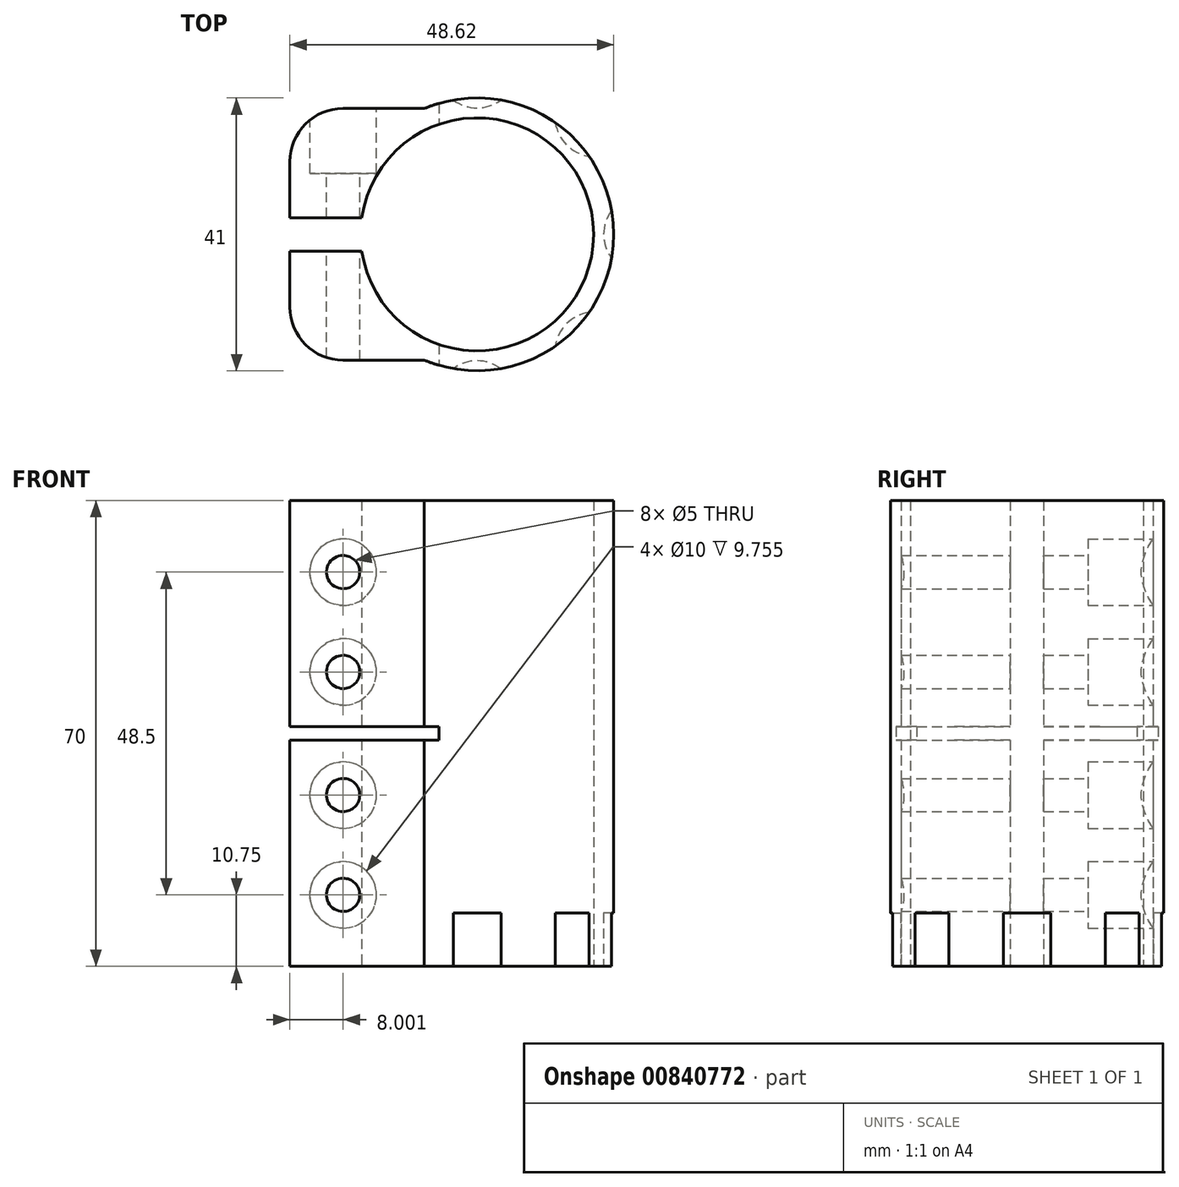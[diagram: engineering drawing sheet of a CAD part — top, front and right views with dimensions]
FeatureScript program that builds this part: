
annotation { "Feature Type Name" : "Feature", "Feature Type Description" : "" }
export const myFeature = defineFeature(function(context is Context, id is Id, definition is map)
    precondition{}
    {
        {
            var Q0;
            Q0=qCreatedBy(makeId("Top.planeOp"),FACE);
            var sketch = newSketch(context, id + "F0", { "sketchPlane" : qUnion([Q0])});
            skArc(sketch, "E0", {"start": v(-17.32, -2.5) * mm, "mid": v(17.5, 0) * mm, "end": v(-17.32, 2.5) * mm});
            skArc(sketch, "E1", {"start": v(-7.92, -18.9) * mm, "mid": v(20.5, 0) * mm, "end": v(-7.92, 18.9) * mm});
            skLineSegment(sketch, "E2", {"start": v(-17.32, 2.5) * mm, "end": v(-28.12, 2.5) * mm});
            skLineSegment(sketch, "E3", {"start": v(-28.12, 2.5) * mm, "end": v(-28.12, 10.9) * mm});
            skLineSegment(sketch, "E4", {"start": v(-20.12, 18.9) * mm, "end": v(-7.92, 18.9) * mm});
            skPoint(sketch, "E5.visualSharp", {"position": v(-28.12, 18.9) * mm});
            skArc(sketch, "E5.filletArc", {"start": v(-20.12, 18.9) * mm, "mid": v(-25.78, 16.57) * mm, "end": v(-28.12, 10.9) * mm});
            skLineSegment(sketch, "E6", {"start": v(0, 0) * mm, "end": v(38.47, 0) * mm, "construction": true});
            skLineSegment(sketch, "E7.MirrorCS", {"start": v(-20.12, -18.9) * mm, "end": v(-7.92, -18.9) * mm});
            skArc(sketch, "E8.MirrorCS", {"start": v(-20.12, -18.9) * mm, "mid": v(-25.78, -16.57) * mm, "end": v(-28.12, -10.9) * mm});
            skLineSegment(sketch, "E9.MirrorCS", {"start": v(-28.12, -2.5) * mm, "end": v(-28.12, -10.9) * mm});
            skLineSegment(sketch, "E10.MirrorCS", {"start": v(-17.32, -2.5) * mm, "end": v(-28.12, -2.5) * mm});
            skSolve(sketch);
        }
        {
            var Q0;
            Q0=makeQuery(id+"F0.imprint","IMPRINT",FACE,{"disambiguationData":[TD([[makeQuery(id+"F0.imprint","IMPRINT",EDGE,{"derivedFrom":sQuery(id+"F0.wireOp",EDGE,"E0")}),-1.0]])]});
            extrude(context, id + "F1", {"entities" : qUnion([Q0]), "endBound" : BoundingType.SYMMETRIC, "depth" : 70 * mm, "offsetDistance" : 25 * mm});
        }
        {
            var Q0;
            Q0=makeQuery(id+"F1.opExtrude","SWEPT_FACE",FACE,{"disambiguationData":[OSD([sQuery(id+"F0.wireOp",EDGE,"E4")])]});
            var sketch = newSketch(context, id + "F2", { "sketchPlane" : qUnion([Q0])});
            skPoint(sketch, "E11", {"position": v(20.12, -24.25) * mm});
            skPoint(sketch, "E12", {"position": v(20.12, -9.25) * mm});
            skPoint(sketch, "E13", {"position": v(20.12, 9.25) * mm});
            skPoint(sketch, "E14", {"position": v(20.12, 24.25) * mm});
            skSolve(sketch);
        }
        {
            var Q0;
            Q0=sQuery(id+"F2.wireOp",VERTEX,"E11");
            var Q1;
            Q1=sQuery(id+"F2.wireOp",VERTEX,"E12");
            var Q2;
            Q2=sQuery(id+"F2.wireOp",VERTEX,"E13");
            var Q3;
            Q3=sQuery(id+"F2.wireOp",VERTEX,"E14");
            var Q4;
            Q4=makeQuery(id+"F1.opExtrude","SWEPT_BODY",BODY,{"disambiguationData":[OSD([sQuery(id+"F0.wireOp",EDGE,"E0"),sQuery(id+"F0.wireOp",EDGE,"E1"),sQuery(id+"F0.wireOp",EDGE,"E2"),sQuery(id+"F0.wireOp",EDGE,"E3"),sQuery(id+"F0.wireOp",EDGE,"E4"),sQuery(id+"F0.wireOp",EDGE,"E5.filletArc"),sQuery(id+"F0.wireOp",EDGE,"E7.MirrorCS"),sQuery(id+"F0.wireOp",EDGE,"E8.MirrorCS"),sQuery(id+"F0.wireOp",EDGE,"E9.MirrorCS"),sQuery(id+"F0.wireOp",EDGE,"E10.MirrorCS")])]});
            hole(context, id + "F3", {"style" : HoleStyle.C_BORE, "endStyle" : HoleEndStyle.THROUGH, "holeDiameter" : 5 * mm, "cBoreDiameter" : 10 * mm, "cBoreDepth" : 8 * mm, "majorDiameter" : 5 * mm, "isTappedThrough" : true, "tappedDepth" : 12 * mm, "tapClearance" : 3, "locations" : qUnion([Q0, Q1, Q2, Q3]), "scope" : qUnion([Q4])});
        }
        {
            var Q0;
            Q0=qCreatedBy(makeId("Front.planeOp"),FACE);
            var sketch = newSketch(context, id + "F4", { "sketchPlane" : qUnion([Q0])});
            skPoint(sketch, "E15.right.end.orphan", {"position": v(-1.39, 0.57) * mm});
            skPoint(sketch, "E15.right.start.orphan", {"position": v(-1.39, -0.6) * mm});
            skPoint(sketch, "E15.left.start.orphan", {"position": v(-14.56, -0.6) * mm});
            skLineSegment(sketch, "E16.bottom", {"start": v(-28.12, -1) * mm, "end": v(-5.72, -1) * mm});
            skLineSegment(sketch, "E16.top", {"start": v(-28.12, 1) * mm, "end": v(-5.72, 1) * mm});
            skLineSegment(sketch, "E16.left", {"start": v(-28.12, -1) * mm, "end": v(-28.12, 1) * mm});
            skLineSegment(sketch, "E16.right", {"start": v(-5.72, -1) * mm, "end": v(-5.72, 1) * mm});
            skSolve(sketch);
        }
        {
            var Q0;
            Q0=makeQuery(id+"F4.imprint","IMPRINT",FACE,{"disambiguationData":[TD([[makeQuery(id+"F4.imprint","IMPRINT",EDGE,{"derivedFrom":sQuery(id+"F4.wireOp",EDGE,"E16.bottom")}),1.0]])]});
            extrude(context, id + "F5", {"entities" : qUnion([Q0]), "operationType" : NewBodyOperationType.REMOVE, "endBound" : BoundingType.SYMMETRIC, "oppositeDirection" : true, "depth" : 50 * mm, "offsetDistance" : 25 * mm});
        }
        {
            var Q0;
            Q0=makeQuery(id+"F1.opExtrude","CAP_FACE",FACE,{"disambiguationData":[OSD([sQuery(id+"F0.wireOp",EDGE,"E0"),sQuery(id+"F0.wireOp",EDGE,"E1"),sQuery(id+"F0.wireOp",EDGE,"E2"),sQuery(id+"F0.wireOp",EDGE,"E3"),sQuery(id+"F0.wireOp",EDGE,"E4"),sQuery(id+"F0.wireOp",EDGE,"E5.filletArc"),sQuery(id+"F0.wireOp",EDGE,"E7.MirrorCS"),sQuery(id+"F0.wireOp",EDGE,"E8.MirrorCS"),sQuery(id+"F0.wireOp",EDGE,"E9.MirrorCS"),sQuery(id+"F0.wireOp",EDGE,"E10.MirrorCS")])],"isStart":true});
            var sketch = newSketch(context, id + "F6", { "sketchPlane" : qUnion([Q0])});
            skCircle(sketch, "E17", {"center": v(0, -25) * mm, "radius": 6 * mm});
            skCircle(sketch, "E18.1.0", {"center": v(17.68, -17.68) * mm, "radius": 6 * mm});
            skCircle(sketch, "E18.2.0", {"center": v(25, 0) * mm, "radius": 6 * mm});
            skCircle(sketch, "E18.3.0", {"center": v(17.68, 17.68) * mm, "radius": 6 * mm});
            skCircle(sketch, "E18.4.0", {"center": v(0, 25) * mm, "radius": 6 * mm});
            skPoint(sketch, "E18.center", {"position": v(0, 0) * mm});
            skLineSegment(sketch, "E18.anchor1", {"start": v(0, 0) * mm, "end": v(0, -25) * mm, "construction": true});
            skLineSegment(sketch, "E18.anchor2", {"start": v(0, 0) * mm, "end": v(0, 25) * mm, "construction": true});
            skSolve(sketch);
        }
        {
            var Q0;
            {var subQ0=sQuery(id+"F6.wireOp",EDGE,"E18.4.0");var subQ1=makeQuery(id+"F1.opExtrude","CAP_EDGE",EDGE,{"disambiguationData":[OSD([sQuery(id+"F0.wireOp",EDGE,"E1")])],"isStart":true});var subQ2=makeQuery(id+"F6.imprint","INTERSECT",VERTEX,{"disambiguationData":[OD(0.0)],"derivedFrom":[subQ1,subQ0]});Q0=makeQuery(id+"F6.imprint","IMPRINT",FACE,{"disambiguationData":[TD([[makeQuery(id+"F6.imprint","IMPRINT",EDGE,{"disambiguationData":[TD([[subQ2,1.0]])],"derivedFrom":subQ0}),1.0]])]});}
            var Q1;
            {var subQ0=sQuery(id+"F6.wireOp",EDGE,"E18.3.0");var subQ1=makeQuery(id+"F1.opExtrude","CAP_EDGE",EDGE,{"disambiguationData":[OSD([sQuery(id+"F0.wireOp",EDGE,"E1")])],"isStart":true});var subQ2=makeQuery(id+"F6.imprint","INTERSECT",VERTEX,{"disambiguationData":[OD(0.0)],"derivedFrom":[subQ1,subQ0]});Q1=makeQuery(id+"F6.imprint","IMPRINT",FACE,{"disambiguationData":[TD([[makeQuery(id+"F6.imprint","IMPRINT",EDGE,{"disambiguationData":[TD([[subQ2,1.0]])],"derivedFrom":subQ0}),1.0]])]});}
            var Q2;
            {var subQ0=sQuery(id+"F6.wireOp",EDGE,"E18.2.0");var subQ1=makeQuery(id+"F1.opExtrude","CAP_EDGE",EDGE,{"disambiguationData":[OSD([sQuery(id+"F0.wireOp",EDGE,"E1")])],"isStart":true});var subQ2=makeQuery(id+"F6.imprint","INTERSECT",VERTEX,{"disambiguationData":[OD(0.0)],"derivedFrom":[subQ1,subQ0]});Q2=makeQuery(id+"F6.imprint","IMPRINT",FACE,{"disambiguationData":[TD([[makeQuery(id+"F6.imprint","IMPRINT",EDGE,{"disambiguationData":[TD([[subQ2,-1.0]])],"derivedFrom":subQ0}),1.0]])]});}
            var Q3;
            {var subQ0=sQuery(id+"F6.wireOp",EDGE,"E18.1.0");var subQ1=makeQuery(id+"F1.opExtrude","CAP_EDGE",EDGE,{"disambiguationData":[OSD([sQuery(id+"F0.wireOp",EDGE,"E1")])],"isStart":true});var subQ2=makeQuery(id+"F6.imprint","INTERSECT",VERTEX,{"disambiguationData":[OD(0.0)],"derivedFrom":[subQ1,subQ0]});Q3=makeQuery(id+"F6.imprint","IMPRINT",FACE,{"disambiguationData":[TD([[makeQuery(id+"F6.imprint","IMPRINT",EDGE,{"disambiguationData":[TD([[subQ2,-1.0]])],"derivedFrom":subQ0}),1.0]])]});}
            var Q4;
            {var subQ0=sQuery(id+"F6.wireOp",EDGE,"E17");var subQ1=makeQuery(id+"F1.opExtrude","CAP_EDGE",EDGE,{"disambiguationData":[OSD([sQuery(id+"F0.wireOp",EDGE,"E1")])],"isStart":true});var subQ2=makeQuery(id+"F6.imprint","INTERSECT",VERTEX,{"disambiguationData":[OD(0.0)],"derivedFrom":[subQ1,subQ0]});Q4=makeQuery(id+"F6.imprint","IMPRINT",FACE,{"disambiguationData":[TD([[makeQuery(id+"F6.imprint","IMPRINT",EDGE,{"disambiguationData":[TD([[subQ2,-1.0]])],"derivedFrom":subQ0}),1.0]])]});}
            var Q5;
            {var subQ0=sQuery(id+"F6.wireOp",EDGE,"E18.4.0");var subQ1=makeQuery(id+"F1.opExtrude","CAP_EDGE",EDGE,{"disambiguationData":[OSD([sQuery(id+"F0.wireOp",EDGE,"E1")])],"isStart":true});var subQ2=makeQuery(id+"F6.imprint","INTERSECT",VERTEX,{"disambiguationData":[OD(0.0)],"derivedFrom":[subQ1,subQ0]});Q5=makeQuery(id+"F6.imprint","IMPRINT",FACE,{"disambiguationData":[TD([[makeQuery(id+"F6.imprint","IMPRINT",EDGE,{"disambiguationData":[TD([[subQ2,-1.0]])],"derivedFrom":subQ0}),1.0]])]});}
            var Q6;
            {var subQ0=sQuery(id+"F6.wireOp",EDGE,"E18.3.0");var subQ1=makeQuery(id+"F1.opExtrude","CAP_EDGE",EDGE,{"disambiguationData":[OSD([sQuery(id+"F0.wireOp",EDGE,"E1")])],"isStart":true});var subQ2=makeQuery(id+"F6.imprint","INTERSECT",VERTEX,{"disambiguationData":[OD(0.0)],"derivedFrom":[subQ1,subQ0]});Q6=makeQuery(id+"F6.imprint","IMPRINT",FACE,{"disambiguationData":[TD([[makeQuery(id+"F6.imprint","IMPRINT",EDGE,{"disambiguationData":[TD([[subQ2,-1.0]])],"derivedFrom":subQ0}),1.0]])]});}
            var Q7;
            {var subQ0=sQuery(id+"F6.wireOp",EDGE,"E18.2.0");var subQ1=makeQuery(id+"F1.opExtrude","CAP_EDGE",EDGE,{"disambiguationData":[OSD([sQuery(id+"F0.wireOp",EDGE,"E1")])],"isStart":true});var subQ2=makeQuery(id+"F6.imprint","INTERSECT",VERTEX,{"disambiguationData":[OD(0.0)],"derivedFrom":[subQ1,subQ0]});Q7=makeQuery(id+"F6.imprint","IMPRINT",FACE,{"disambiguationData":[TD([[makeQuery(id+"F6.imprint","IMPRINT",EDGE,{"disambiguationData":[TD([[subQ2,1.0]])],"derivedFrom":subQ0}),1.0]])]});}
            var Q8;
            {var subQ0=sQuery(id+"F6.wireOp",EDGE,"E18.1.0");var subQ1=makeQuery(id+"F1.opExtrude","CAP_EDGE",EDGE,{"disambiguationData":[OSD([sQuery(id+"F0.wireOp",EDGE,"E1")])],"isStart":true});var subQ2=makeQuery(id+"F6.imprint","INTERSECT",VERTEX,{"disambiguationData":[OD(0.0)],"derivedFrom":[subQ1,subQ0]});Q8=makeQuery(id+"F6.imprint","IMPRINT",FACE,{"disambiguationData":[TD([[makeQuery(id+"F6.imprint","IMPRINT",EDGE,{"disambiguationData":[TD([[subQ2,1.0]])],"derivedFrom":subQ0}),1.0]])]});}
            var Q9;
            {var subQ0=sQuery(id+"F6.wireOp",EDGE,"E17");var subQ1=makeQuery(id+"F1.opExtrude","CAP_EDGE",EDGE,{"disambiguationData":[OSD([sQuery(id+"F0.wireOp",EDGE,"E1")])],"isStart":true});var subQ2=makeQuery(id+"F6.imprint","INTERSECT",VERTEX,{"disambiguationData":[OD(0.0)],"derivedFrom":[subQ1,subQ0]});Q9=makeQuery(id+"F6.imprint","IMPRINT",FACE,{"disambiguationData":[TD([[makeQuery(id+"F6.imprint","IMPRINT",EDGE,{"disambiguationData":[TD([[subQ2,1.0]])],"derivedFrom":subQ0}),1.0]])]});}
            extrude(context, id + "F7", {"entities" : qUnion([Q0, Q1, Q2, Q3, Q4, Q5, Q6, Q7, Q8, Q9]), "operationType" : NewBodyOperationType.REMOVE, "oppositeDirection" : true, "depth" : 8 * mm, "offsetDistance" : 25 * mm});
        }
    });
